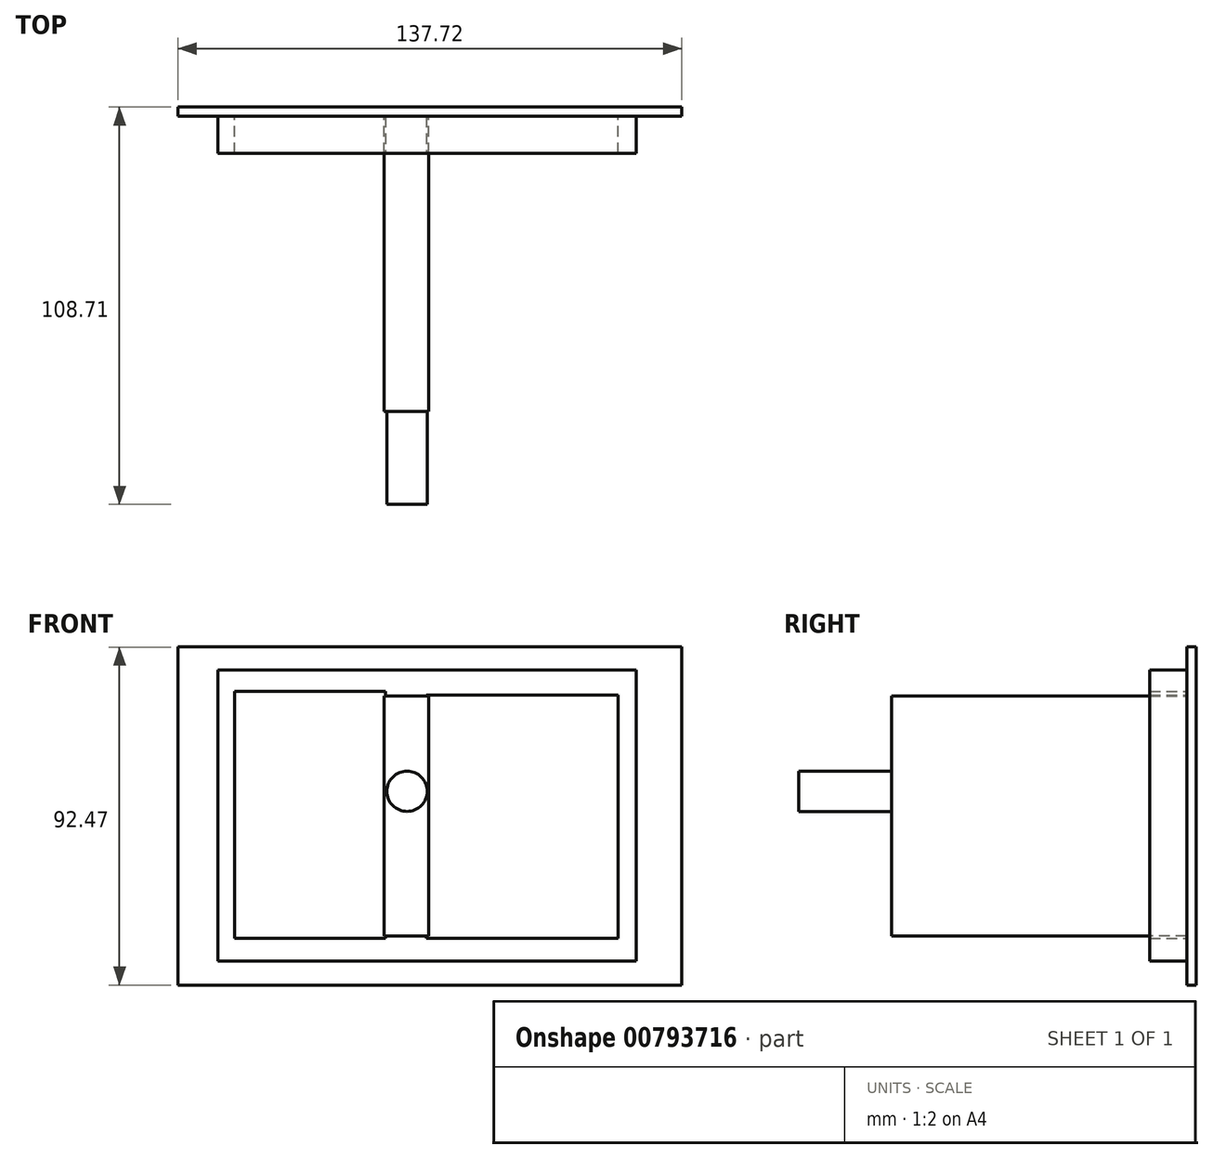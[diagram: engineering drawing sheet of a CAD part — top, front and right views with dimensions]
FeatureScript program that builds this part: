
annotation { "Feature Type Name" : "Feature", "Feature Type Description" : "" }
export const myFeature = defineFeature(function(context is Context, id is Id, definition is map)
    precondition{}
    {
        {
            var Q0;
            Q0=qCreatedBy(makeId("Front.planeOp"),FACE);
            var sketch = newSketch(context, id + "F0", { "sketchPlane" : qUnion([Q0])});
            skLineSegment(sketch, "E0.bottom", {"start": v(-51.8, 52.3) * mm, "end": v(62.63, 52.3) * mm});
            skLineSegment(sketch, "E0.top", {"start": v(-51.8, -27.38) * mm, "end": v(62.63, -27.38) * mm});
            skLineSegment(sketch, "E0.left", {"start": v(-51.8, 52.3) * mm, "end": v(-51.8, -27.38) * mm});
            skLineSegment(sketch, "E0.right", {"start": v(62.63, 52.3) * mm, "end": v(62.63, -27.38) * mm});
            skLineSegment(sketch, "E1", {"start": v(0, 52.3) * mm, "end": v(0, -27.38) * mm});
            skLineSegment(sketch, "E2.bottom", {"start": v(-47.22, 46.4) * mm, "end": v(-5.9, 46.4) * mm});
            skLineSegment(sketch, "E2.top", {"start": v(-47.22, -21.15) * mm, "end": v(-5.9, -21.15) * mm});
            skLineSegment(sketch, "E2.left", {"start": v(-47.22, 46.4) * mm, "end": v(-47.22, -21.15) * mm});
            skLineSegment(sketch, "E2.right", {"start": v(-5.9, 46.4) * mm, "end": v(-5.9, -21.15) * mm});
            skLineSegment(sketch, "E3.bottom", {"start": v(5.25, 45.42) * mm, "end": v(57.71, 45.42) * mm});
            skLineSegment(sketch, "E3.top", {"start": v(5.25, -21.15) * mm, "end": v(57.71, -21.15) * mm});
            skLineSegment(sketch, "E3.left", {"start": v(5.25, 45.42) * mm, "end": v(5.25, -21.15) * mm});
            skLineSegment(sketch, "E3.right", {"start": v(57.71, 45.42) * mm, "end": v(57.71, -21.15) * mm});
            skSolve(sketch);
        }
        {
            var Q0;
            Q0 = qSketchRegion(id + "F0", true);
            extrude(context, id + "F1", {"entities" : qUnion([Q0]), "depth" : 12.7 * mm, "offsetDistance" : 25.4 * mm});
        }
        {
            var Q0;
            Q0=qCreatedBy(makeId("Front.planeOp"),FACE);
            var sketch = newSketch(context, id + "F2", { "sketchPlane" : qUnion([Q0])});
            skLineSegment(sketch, "E4.bottom", {"start": v(-62.63, 58.53) * mm, "end": v(75.1, 58.53) * mm});
            skLineSegment(sketch, "E4.top", {"start": v(-62.63, -33.94) * mm, "end": v(75.1, -33.94) * mm});
            skLineSegment(sketch, "E4.left", {"start": v(-62.63, 58.53) * mm, "end": v(-62.63, -33.94) * mm});
            skLineSegment(sketch, "E4.right", {"start": v(75.1, 58.53) * mm, "end": v(75.1, -33.94) * mm});
            skSolve(sketch);
        }
        {
            var Q0;
            Q0 = qSketchRegion(id + "F2", true);
            extrude(context, id + "F3", {"entities" : qUnion([Q0]), "operationType" : NewBodyOperationType.ADD, "depth" : 2.54 * mm, "offsetDistance" : 25.4 * mm});
        }
        {
            var Q0;
            Q0=qCreatedBy(makeId("Front.planeOp"),FACE);
            var sketch = newSketch(context, id + "F4", { "sketchPlane" : qUnion([Q0])});
            skLineSegment(sketch, "E5", {"start": v(-6.23, -20.5) * mm, "end": v(5.9, -20.5) * mm});
            skLineSegment(sketch, "E6", {"start": v(5.9, -20.5) * mm, "end": v(5.9, 45.09) * mm});
            skLineSegment(sketch, "E7", {"start": v(5.9, 45.09) * mm, "end": v(-6.23, 45.09) * mm});
            skLineSegment(sketch, "E8", {"start": v(-6.23, 45.09) * mm, "end": v(-6.23, -20.5) * mm});
            skSolve(sketch);
        }
        {
            var Q0;
            Q0 = qSketchRegion(id + "F4", true);
            extrude(context, id + "F5", {"entities" : qUnion([Q0]), "operationType" : NewBodyOperationType.ADD, "depth" : 83.31 * mm, "offsetDistance" : 25.4 * mm});
        }
        {
            var Q0;
            Q0=qCreatedBy(makeId("Front.planeOp"),FACE);
            var sketch = newSketch(context, id + "F6", { "sketchPlane" : qUnion([Q0])});
            skCircle(sketch, "E9", {"center": v(0, 19.06) * mm, "radius": 5.5 * mm});
            skSolve(sketch);
        }
        {
            var Q0;
            Q0 = qSketchRegion(id + "F6", true);
            extrude(context, id + "F7", {"entities" : qUnion([Q0]), "operationType" : NewBodyOperationType.ADD, "depth" : 108.7 * mm, "offsetDistance" : 25.4 * mm});
        }
    });
